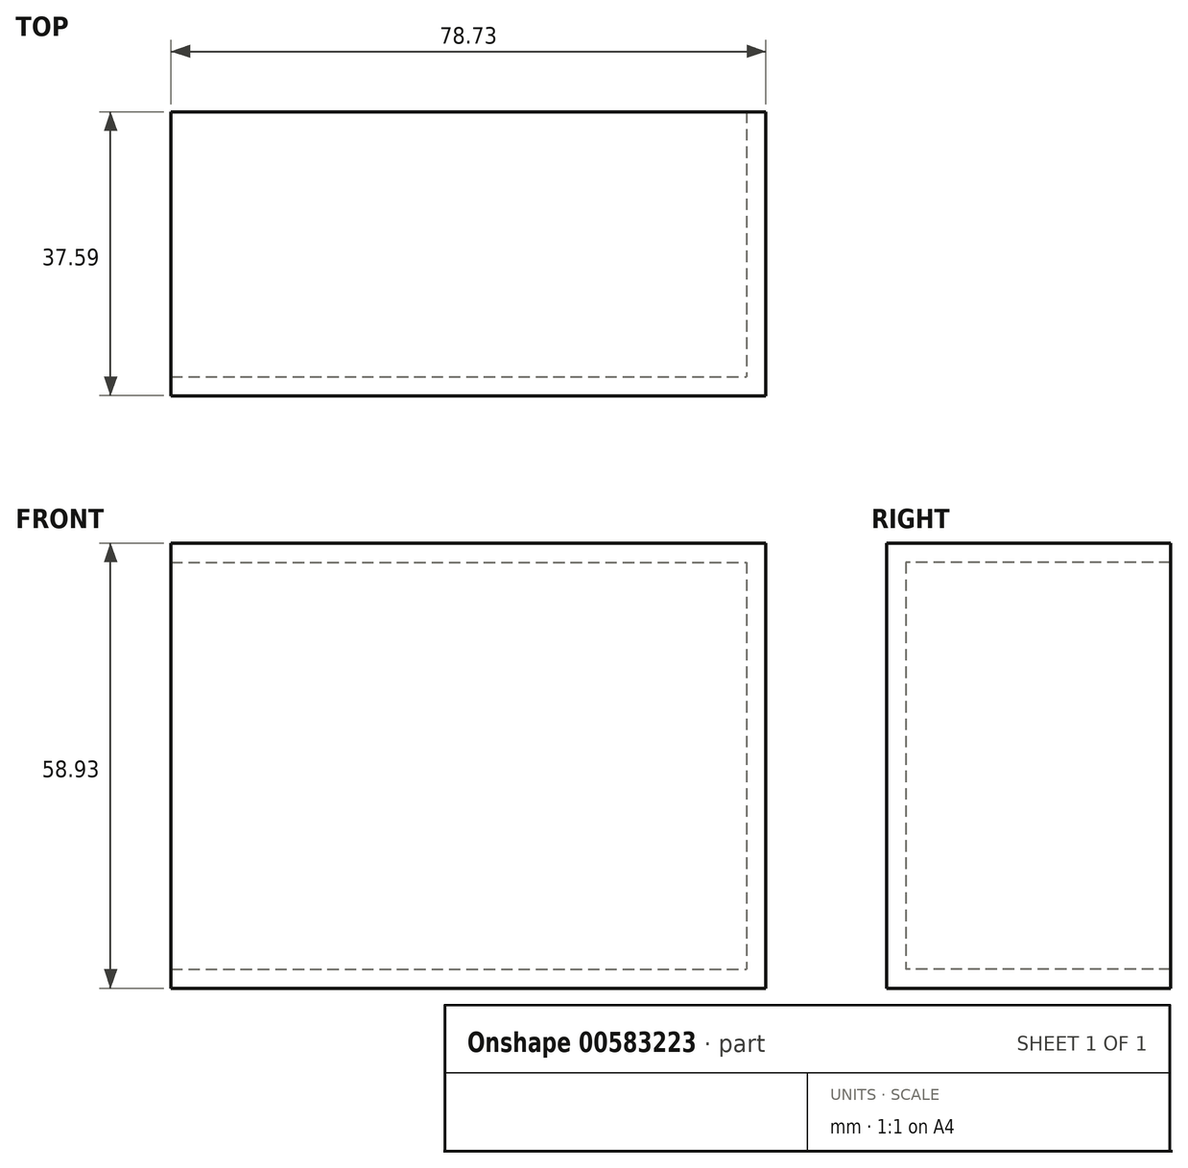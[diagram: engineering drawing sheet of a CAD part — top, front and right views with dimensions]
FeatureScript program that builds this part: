
annotation { "Feature Type Name" : "Feature", "Feature Type Description" : "" }
export const myFeature = defineFeature(function(context is Context, id is Id, definition is map)
    precondition{}
    {
        {
            var Q0;
            Q0=qCreatedBy(makeId("Top.planeOp"),FACE);
            var sketch = newSketch(context, id + "F0", { "sketchPlane" : qUnion([Q0])});
            skLineSegment(sketch, "E0.bottom", {"start": v(-40.87, -16.95) * mm, "end": v(37.86, -16.95) * mm});
            skLineSegment(sketch, "E0.top", {"start": v(-40.87, -54.54) * mm, "end": v(37.86, -54.54) * mm});
            skLineSegment(sketch, "E0.left", {"start": v(-40.87, -16.95) * mm, "end": v(-40.87, -54.54) * mm});
            skLineSegment(sketch, "E0.right", {"start": v(37.86, -16.95) * mm, "end": v(37.86, -54.54) * mm});
            skSolve(sketch);
        }
        {
            var Q0;
            Q0=makeQuery(id+"F0.imprint","IMPRINT",FACE,{"disambiguationData":[TD([[makeQuery(id+"F0.imprint","IMPRINT",EDGE,{"derivedFrom":sQuery(id+"F0.wireOp",EDGE,"E0.bottom")}),-1.0]])]});
            extrude(context, id + "F1", {"entities" : qUnion([Q0]), "depth" : 58.93 * mm, "offsetDistance" : 25.4 * mm});
        }
        {
            var Q0;
            Q0=makeQuery(id+"F1.opExtrude","SWEPT_FACE",FACE,{"disambiguationData":[OSD([sQuery(id+"F0.wireOp",EDGE,"E0.bottom")])]});
            var Q1;
            Q1=makeQuery(id+"F1.opExtrude","SWEPT_FACE",FACE,{"disambiguationData":[OSD([sQuery(id+"F0.wireOp",EDGE,"E0.left")])]});
            shell(context, id + "F2", {"entities" : qUnion([Q0, Q1]), "thickness" : 2.54 * mm});
        }
    });
